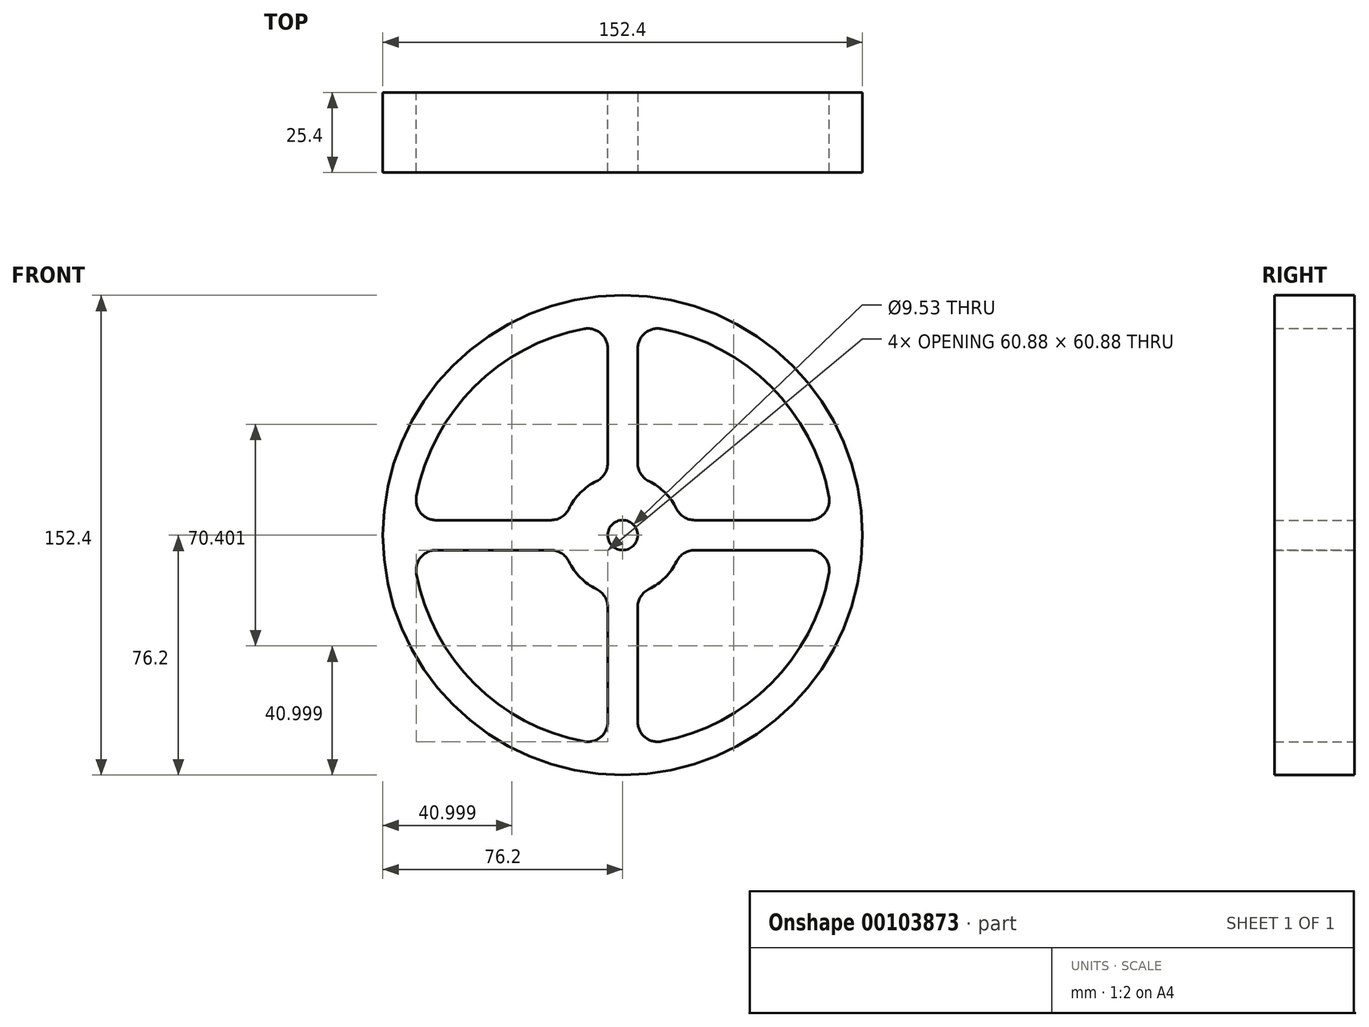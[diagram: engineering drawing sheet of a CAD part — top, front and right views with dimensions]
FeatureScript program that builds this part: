
annotation { "Feature Type Name" : "Feature", "Feature Type Description" : "" }
export const myFeature = defineFeature(function(context is Context, id is Id, definition is map)
    precondition{}
    {
        {
            var Q0;
            Q0=qCreatedBy(makeId("Front.planeOp"),FACE);
            var sketch = newSketch(context, id + "F0", { "sketchPlane" : qUnion([Q0])});
            skCircle(sketch, "E0", {"center": v(0, 0) * mm, "radius": 76.2 * mm});
            skCircle(sketch, "E1", {"center": v(0, 0) * mm, "radius": 66.68 * mm});
            skCircle(sketch, "E2", {"center": v(0, 0) * mm, "radius": 19.05 * mm});
            skLineSegment(sketch, "E3", {"start": v(-4.76, 66.5) * mm, "end": v(-4.76, 18.45) * mm});
            skLineSegment(sketch, "E4", {"start": v(-66.5, 4.76) * mm, "end": v(-18.45, 4.76) * mm});
            skLineSegment(sketch, "E5.MirrorCS", {"start": v(4.76, 66.5) * mm, "end": v(4.76, 18.45) * mm});
            skLineSegment(sketch, "E6.MirrorCS", {"start": v(66.5, 4.76) * mm, "end": v(18.45, 4.76) * mm});
            skLineSegment(sketch, "E7.MirrorCS", {"start": v(-66.5, -4.76) * mm, "end": v(-18.45, -4.76) * mm});
            skLineSegment(sketch, "E8.MirrorCS", {"start": v(66.5, -4.76) * mm, "end": v(18.45, -4.76) * mm});
            skLineSegment(sketch, "E9.MirrorCS", {"start": v(4.76, -66.5) * mm, "end": v(4.76, -18.45) * mm});
            skLineSegment(sketch, "E10.MirrorCS", {"start": v(-4.76, -66.5) * mm, "end": v(-4.76, -18.45) * mm});
            skCircle(sketch, "E11", {"center": v(0, 0) * mm, "radius": 4.76 * mm});
            skSolve(sketch);
        }
        {
            var Q0;
            Q0=makeQuery(id+"F0.imprint","IMPRINT",FACE,{"disambiguationData":[TD([[makeQuery(id+"F0.imprint","IMPRINT",EDGE,{"derivedFrom":sQuery(id+"F0.wireOp",EDGE,"E0")}),1.0]])]});
            var Q1;
            {var subQ0=sQuery(id+"F0.wireOp",EDGE,"E3");Q1=makeQuery(id+"F0.imprint","IMPRINT",FACE,{"disambiguationData":[TD([[makeQuery(id+"F0.imprint","IMPRINT",EDGE,{"derivedFrom":subQ0}),1.0]])]});}
            var Q2;
            {var subQ0=sQuery(id+"F0.wireOp",EDGE,"E6.MirrorCS");Q2=makeQuery(id+"F0.imprint","IMPRINT",FACE,{"disambiguationData":[TD([[makeQuery(id+"F0.imprint","IMPRINT",EDGE,{"derivedFrom":subQ0}),1.0]])]});}
            var Q3;
            {var subQ0=sQuery(id+"F0.wireOp",EDGE,"E2");var subQ6=makeQuery(id+"F0.imprint","INTERSECT",VERTEX,{"derivedFrom":[subQ0,sQuery(id+"F0.wireOp",EDGE,"E5.MirrorCS")]});Q3=makeQuery(id+"F0.imprint","IMPRINT",FACE,{"disambiguationData":[TD([[makeQuery(id+"F0.imprint","IMPRINT",EDGE,{"disambiguationData":[TD([[subQ6,1.0]])],"derivedFrom":subQ0}),1.0]])]});}
            var Q4;
            {var subQ0=sQuery(id+"F0.wireOp",EDGE,"E9.MirrorCS");Q4=makeQuery(id+"F0.imprint","IMPRINT",FACE,{"disambiguationData":[TD([[makeQuery(id+"F0.imprint","IMPRINT",EDGE,{"derivedFrom":subQ0}),1.0]])]});}
            var Q5;
            {var subQ0=sQuery(id+"F0.wireOp",EDGE,"E4");Q5=makeQuery(id+"F0.imprint","IMPRINT",FACE,{"disambiguationData":[TD([[makeQuery(id+"F0.imprint","IMPRINT",EDGE,{"derivedFrom":subQ0}),-1.0]])]});}
            extrude(context, id + "F1", {"entities" : qUnion([Q0, Q1, Q2, Q3, Q4, Q5]), "depth" : 25.4 * mm});
        }
        {
            var Q0;
            Q0=makeQuery(id+"F1.opExtrude","SWEPT_EDGE",EDGE,{"disambiguationData":[OSD([sQuery(id+"F0.wireOp",EDGE,"E2"),sQuery(id+"F0.wireOp",EDGE,"E5.MirrorCS")])]});
            var Q1;
            Q1=makeQuery(id+"F1.opExtrude","SWEPT_EDGE",EDGE,{"disambiguationData":[OSD([sQuery(id+"F0.wireOp",EDGE,"E2"),sQuery(id+"F0.wireOp",EDGE,"E6.MirrorCS")])]});
            var Q2;
            Q2=makeQuery(id+"F1.opExtrude","SWEPT_EDGE",EDGE,{"disambiguationData":[OSD([sQuery(id+"F0.wireOp",EDGE,"E1"),sQuery(id+"F0.wireOp",EDGE,"E4")])]});
            var Q3;
            Q3=makeQuery(id+"F1.opExtrude","SWEPT_EDGE",EDGE,{"disambiguationData":[OSD([sQuery(id+"F0.wireOp",EDGE,"E1"),sQuery(id+"F0.wireOp",EDGE,"E9.MirrorCS")])]});
            var Q4;
            Q4=makeQuery(id+"F1.opExtrude","SWEPT_EDGE",EDGE,{"disambiguationData":[OSD([sQuery(id+"F0.wireOp",EDGE,"E2"),sQuery(id+"F0.wireOp",EDGE,"E4")])]});
            var Q5;
            Q5=makeQuery(id+"F1.opExtrude","SWEPT_EDGE",EDGE,{"disambiguationData":[OSD([sQuery(id+"F0.wireOp",EDGE,"E2"),sQuery(id+"F0.wireOp",EDGE,"E3")])]});
            var Q6;
            Q6=makeQuery(id+"F1.opExtrude","SWEPT_EDGE",EDGE,{"disambiguationData":[OSD([sQuery(id+"F0.wireOp",EDGE,"E1"),sQuery(id+"F0.wireOp",EDGE,"E10.MirrorCS")])]});
            var Q7;
            Q7=makeQuery(id+"F1.opExtrude","SWEPT_EDGE",EDGE,{"disambiguationData":[OSD([sQuery(id+"F0.wireOp",EDGE,"E1"),sQuery(id+"F0.wireOp",EDGE,"E6.MirrorCS")])]});
            var Q8;
            Q8=makeQuery(id+"F1.opExtrude","SWEPT_EDGE",EDGE,{"disambiguationData":[OSD([sQuery(id+"F0.wireOp",EDGE,"E2"),sQuery(id+"F0.wireOp",EDGE,"E8.MirrorCS")])]});
            var Q9;
            Q9=makeQuery(id+"F1.opExtrude","SWEPT_EDGE",EDGE,{"disambiguationData":[OSD([sQuery(id+"F0.wireOp",EDGE,"E2"),sQuery(id+"F0.wireOp",EDGE,"E9.MirrorCS")])]});
            var Q10;
            Q10=makeQuery(id+"F1.opExtrude","SWEPT_EDGE",EDGE,{"disambiguationData":[OSD([sQuery(id+"F0.wireOp",EDGE,"E1"),sQuery(id+"F0.wireOp",EDGE,"E5.MirrorCS")])]});
            var Q11;
            Q11=makeQuery(id+"F1.opExtrude","SWEPT_EDGE",EDGE,{"disambiguationData":[OSD([sQuery(id+"F0.wireOp",EDGE,"E1"),sQuery(id+"F0.wireOp",EDGE,"E7.MirrorCS")])]});
            var Q12;
            Q12=makeQuery(id+"F1.opExtrude","SWEPT_EDGE",EDGE,{"disambiguationData":[OSD([sQuery(id+"F0.wireOp",EDGE,"E2"),sQuery(id+"F0.wireOp",EDGE,"E10.MirrorCS")])]});
            var Q13;
            Q13=makeQuery(id+"F1.opExtrude","SWEPT_EDGE",EDGE,{"disambiguationData":[OSD([sQuery(id+"F0.wireOp",EDGE,"E2"),sQuery(id+"F0.wireOp",EDGE,"E7.MirrorCS")])]});
            var Q14;
            Q14=makeQuery(id+"F1.opExtrude","SWEPT_EDGE",EDGE,{"disambiguationData":[OSD([sQuery(id+"F0.wireOp",EDGE,"E1"),sQuery(id+"F0.wireOp",EDGE,"E3")])]});
            var Q15;
            Q15=makeQuery(id+"F1.opExtrude","SWEPT_EDGE",EDGE,{"disambiguationData":[OSD([sQuery(id+"F0.wireOp",EDGE,"E1"),sQuery(id+"F0.wireOp",EDGE,"E8.MirrorCS")])]});
            fillet(context, id + "F2", {"entities" : qUnion([Q0, Q1, Q2, Q3, Q4, Q5, Q6, Q7, Q8, Q9, Q10, Q11, Q12, Q13, Q14, Q15]), "radius" : 6.35 * mm, "tangentPropagation" : true, "allowEdgeOverflow" : false});
        }
    });
